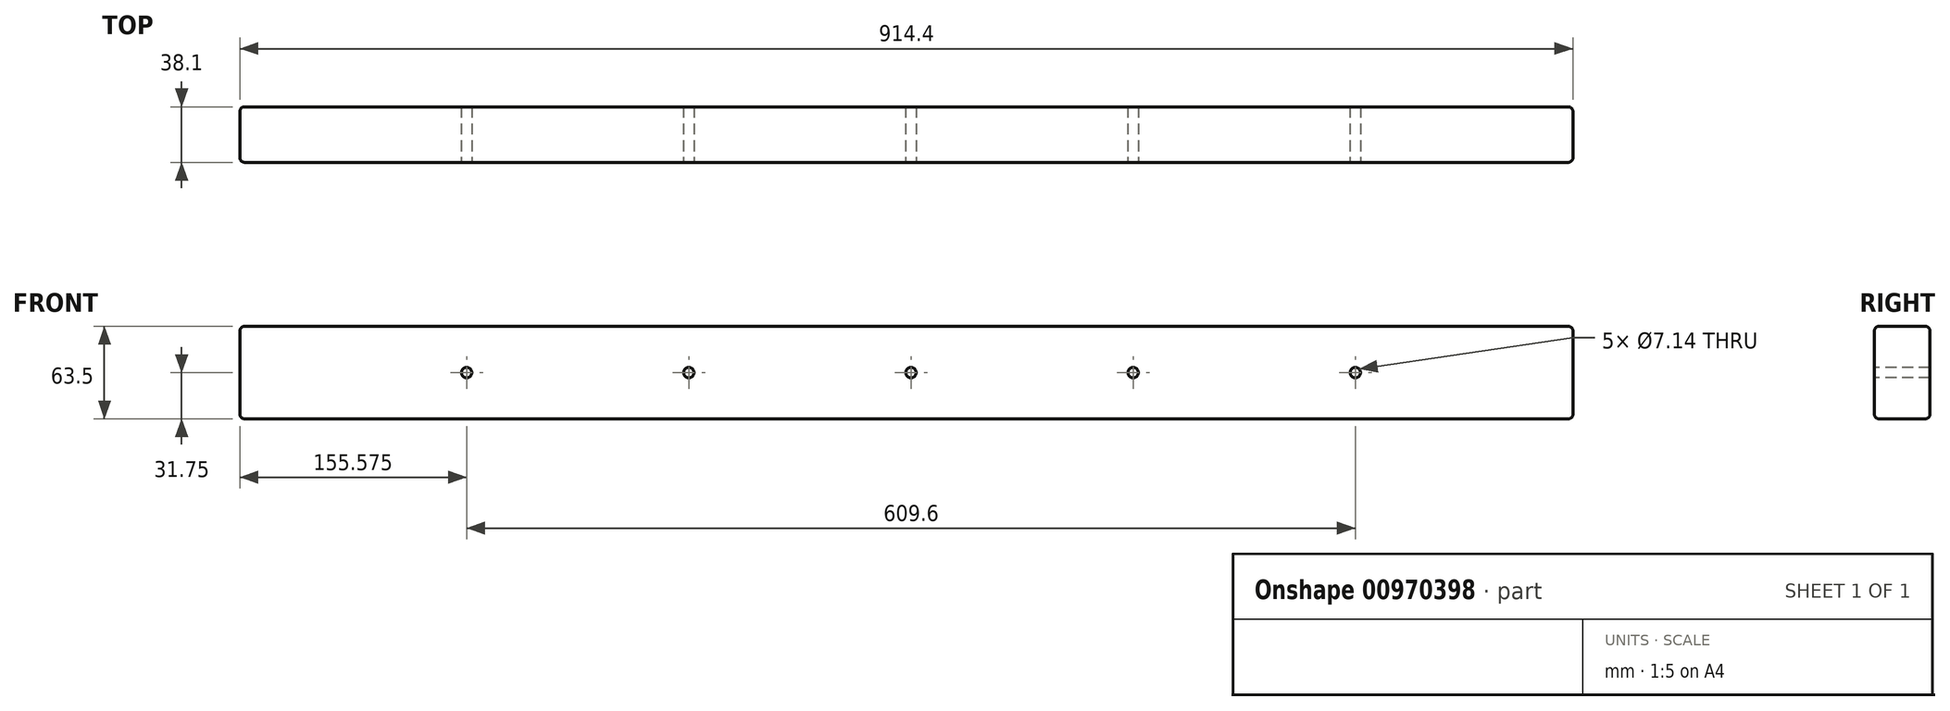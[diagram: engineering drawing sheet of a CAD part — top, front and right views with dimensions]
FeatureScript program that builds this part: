
annotation { "Feature Type Name" : "Feature", "Feature Type Description" : "" }
export const myFeature = defineFeature(function(context is Context, id is Id, definition is map)
    precondition{}
    {
        {
            var Q0;
            Q0=qCreatedBy(makeId("Front.planeOp"),FACE);
            var sketch = newSketch(context, id + "F0", { "sketchPlane" : qUnion([Q0])});
            skLineSegment(sketch, "E0.bottom", {"start": v(0, 0) * mm, "end": v(914.4, 0) * mm});
            skLineSegment(sketch, "E0.top", {"start": v(0, -63.5) * mm, "end": v(914.4, -63.5) * mm});
            skLineSegment(sketch, "E0.left", {"start": v(0, 0) * mm, "end": v(0, -63.5) * mm});
            skLineSegment(sketch, "E0.right", {"start": v(914.4, 0) * mm, "end": v(914.4, -63.5) * mm});
            skSolve(sketch);
        }
        {
            var Q0;
            Q0 = qSketchRegion(id + "F0", true);
            extrude(context, id + "F1", {"entities" : qUnion([Q0]), "depth" : 38.1 * mm, "offsetDistance" : 25.4 * mm});
        }
        {
            var Q0;
            Q0=makeQuery(id+"F1.opExtrude","CAP_EDGE",EDGE,{"disambiguationData":[OSD([sQuery(id+"F0.wireOp",EDGE,"E0.bottom")])],"isStart":false});
            var Q1;
            Q1=makeQuery(id+"F1.opExtrude","CAP_EDGE",EDGE,{"disambiguationData":[OSD([sQuery(id+"F0.wireOp",EDGE,"E0.bottom")])],"isStart":true});
            var Q2;
            Q2=makeQuery(id+"F1.opExtrude","CAP_EDGE",EDGE,{"disambiguationData":[OSD([sQuery(id+"F0.wireOp",EDGE,"E0.top")])],"isStart":false});
            var Q3;
            Q3=makeQuery(id+"F1.opExtrude","CAP_EDGE",EDGE,{"disambiguationData":[OSD([sQuery(id+"F0.wireOp",EDGE,"E0.left")])],"isStart":true});
            var Q4;
            Q4=makeQuery(id+"F1.opExtrude","CAP_EDGE",EDGE,{"disambiguationData":[OSD([sQuery(id+"F0.wireOp",EDGE,"E0.left")])],"isStart":false});
            var Q5;
            Q5=makeQuery(id+"F1.opExtrude","SWEPT_EDGE",EDGE,{"disambiguationData":[OSD([sQuery(id+"F0.wireOp",EDGE,"E0.bottom"),sQuery(id+"F0.wireOp",EDGE,"E0.left")])]});
            var Q6;
            Q6=makeQuery(id+"F1.opExtrude","SWEPT_EDGE",EDGE,{"disambiguationData":[OSD([sQuery(id+"F0.wireOp",EDGE,"E0.top"),sQuery(id+"F0.wireOp",EDGE,"E0.left")])]});
            var Q7;
            Q7=makeQuery(id+"F1.opExtrude","CAP_EDGE",EDGE,{"disambiguationData":[OSD([sQuery(id+"F0.wireOp",EDGE,"E0.top")])],"isStart":true});
            var Q8;
            Q8=makeQuery(id+"F1.opExtrude","SWEPT_EDGE",EDGE,{"disambiguationData":[OSD([sQuery(id+"F0.wireOp",EDGE,"E0.top"),sQuery(id+"F0.wireOp",EDGE,"E0.right")])]});
            var Q9;
            Q9=makeQuery(id+"F1.opExtrude","CAP_EDGE",EDGE,{"disambiguationData":[OSD([sQuery(id+"F0.wireOp",EDGE,"E0.right")])],"isStart":true});
            var Q10;
            Q10=makeQuery(id+"F1.opExtrude","SWEPT_EDGE",EDGE,{"disambiguationData":[OSD([sQuery(id+"F0.wireOp",EDGE,"E0.bottom"),sQuery(id+"F0.wireOp",EDGE,"E0.right")])]});
            var Q11;
            Q11=makeQuery(id+"F1.opExtrude","CAP_EDGE",EDGE,{"disambiguationData":[OSD([sQuery(id+"F0.wireOp",EDGE,"E0.right")])],"isStart":false});
            fillet(context, id + "F2", {"entities" : qUnion([Q0, Q1, Q2, Q3, Q4, Q5, Q6, Q7, Q8, Q9, Q10, Q11]), "radius" : 3.17 * mm, "tangentPropagation" : true, "allowEdgeOverflow" : false});
        }
        {
            var Q0;
            Q0=makeQuery(id+"F1.opExtrude","CAP_FACE",FACE,{"disambiguationData":[OSD([sQuery(id+"F0.wireOp",EDGE,"E0.bottom"),sQuery(id+"F0.wireOp",EDGE,"E0.top"),sQuery(id+"F0.wireOp",EDGE,"E0.left"),sQuery(id+"F0.wireOp",EDGE,"E0.right")])],"isStart":false});
            var sketch = newSketch(context, id + "F3", { "sketchPlane" : qUnion([Q0])});
            skPoint(sketch, "E1", {"position": v(155.57, -31.75) * mm});
            skPoint(sketch, "E1.positionSnap0", {"position": v(3.17, -31.75) * mm});
            skPoint(sketch, "E2", {"position": v(307.98, -31.75) * mm});
            skPoint(sketch, "E3", {"position": v(460.38, -31.75) * mm});
            skPoint(sketch, "E4", {"position": v(612.77, -31.75) * mm});
            skPoint(sketch, "E5", {"position": v(765.17, -31.75) * mm});
            skSolve(sketch);
        }
        {
            var Q0;
            Q0=sQuery(id+"F3.wireOp",VERTEX,"E1");
            var Q1;
            Q1=sQuery(id+"F3.wireOp",VERTEX,"E2");
            var Q2;
            Q2=sQuery(id+"F3.wireOp",VERTEX,"E4");
            var Q3;
            Q3=sQuery(id+"F3.wireOp",VERTEX,"E3");
            var Q4;
            Q4=sQuery(id+"F3.wireOp",VERTEX,"E5");
            var Q5;
            Q5=makeQuery(id+"F1.opExtrude","SWEPT_BODY",BODY,{"disambiguationData":[OSD([sQuery(id+"F0.wireOp",EDGE,"E0.bottom"),sQuery(id+"F0.wireOp",EDGE,"E0.top"),sQuery(id+"F0.wireOp",EDGE,"E0.left"),sQuery(id+"F0.wireOp",EDGE,"E0.right")])]});
            hole(context, id + "F4", {"style" : HoleStyle.SIMPLE, "endStyle" : HoleEndStyle.THROUGH, "standardTappedOrClearance" : lookupTablePath({ "fit" : "Normal (ASME)", "standard" : "ANSI", "size" : "1/4", "type" : "Clearance" }), "standardBlindInLast" : lookupTablePath({ "fit" : "Normal", "standard" : "ANSI", "engagement" : "75%", "pitch" : "20 tpi", "size" : "1/4", "type" : "Clearance & tapped" }), "holeDiameter" : 7.14 * mm, "majorDiameter" : 6.35 * mm, "isTappedThrough" : true, "tappedDepth" : 12.7 * mm, "tapClearance" : 3, "locations" : qUnion([Q0, Q1, Q2, Q3, Q4]), "scope" : qUnion([Q5])});
        }
    });
